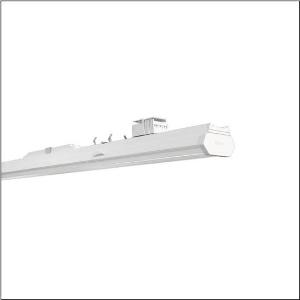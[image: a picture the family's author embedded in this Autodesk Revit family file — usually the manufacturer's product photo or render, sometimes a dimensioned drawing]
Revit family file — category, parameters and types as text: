
# Revit family: licross_r__11_protected_mo_51tp11dn695g_68fa
name_source: partatom
category: Lighting Fixtures
units: mm (PartAtom-declared; Revit-internal decimal feet)

## family parameters
Cut with Voids When Loaded = No
Host = Face
Light Source = No
Part Type = Normal
Room Calculation Point = No
Round Connector Dimension = Use Diameter
Shared = No

## types (1)
- --- (1 x LED, 9680 lm, 57.1 W, 6500K)
    Apparent Load = 57 VA
    CIE Flux Codes = 83 94 98 100 100
    Color Rendering = 80
    Color Temperature = 6500K
    Default Elevation = 1800 mm
    Description = Licross® 11 Protected MO, luminaire insert, of sheet steel, galvanised, coil coated, white, length: 1.500mm, width: 90mm, height: 101mm, LED rated luminous flux: 9.680lm, light colour: 865, control gear: DALI 2, with plug, 5-pole, with phase selection, mains connection: 220..240V, AC, 50/60Hz, rated input power: 57W, halogen-free wiring, primary light control with lens, of plastic, primary optical cover: cover, of PMMA, light emission: direct distribution, primary light characteristic: symmetric, protection rating (complete): IP64, insulation class (complete): insulation class I (protective earthing), certification: CE, ENEC, VDE, UKCA, protection symbol: D if used in an environment with conductive dust loads with corresponding accessories, impact resistance: IK06, permissible ambient temperature for indoor applications: -25..+35°C, corresponds to IFS (International Featured Standards) requirements for safety and quality in the food industry, reducing of maximum allowable ambient temperature of 5°C with ceiling mounting, LABS conformity tested according to VDMA 24364:2018-05, packaging unit: 1 piece
    Height = 92 mm
    Lamp = 1 x LED
    Lamp Light Flux = 9680 lm
    Lamp Power = 57.1 W
    Lamp count = 1
    Length = 1500 mm
    Luminous efficacy = 170 lm/W
    Manufacturer = Siteco
    ModVariant = No
    Model = 51TP11DN695G
    Mounting Place = Ceiling
    Mounting Type = Pendant
    Number of Poles = 1
    OnlyDefault = Yes
    Power Factor = 1
    Product Name = Licross® 11 Protected MO
    Product group = luminaire insert
    ProductGroupID = 901
    Protection Class = Protection class I
    Protection Degree = IP 64
    RLX_Detail_Level = 1
    RLX_Emergency_Light_Flux = 0 lm
    RLX_Emergency_Type = 0
    RLX_Emergency_Type_DB = No
    RlxData = <blob elided: 24109 chars, md5=2ba1532a>
    Socket = socket
    Standby Power = 0 W
    System Light Flux = 9680 lm
    System Power = 57 W
    Type Comments = factory setting: luminous flux: 100 % | dim-lin: 254 | 378 mA
    Type Image = l_1256148.jpg
    URL = http://relux.com
    VarID = @adj_015689
    Voltage = 0 V
    Weight = 0.00 kg
    Width = 88 mm

## geometry (parser evidence)
native form markers: Blend x4, Sweep x9
no freeform markers — native parametric forms only
